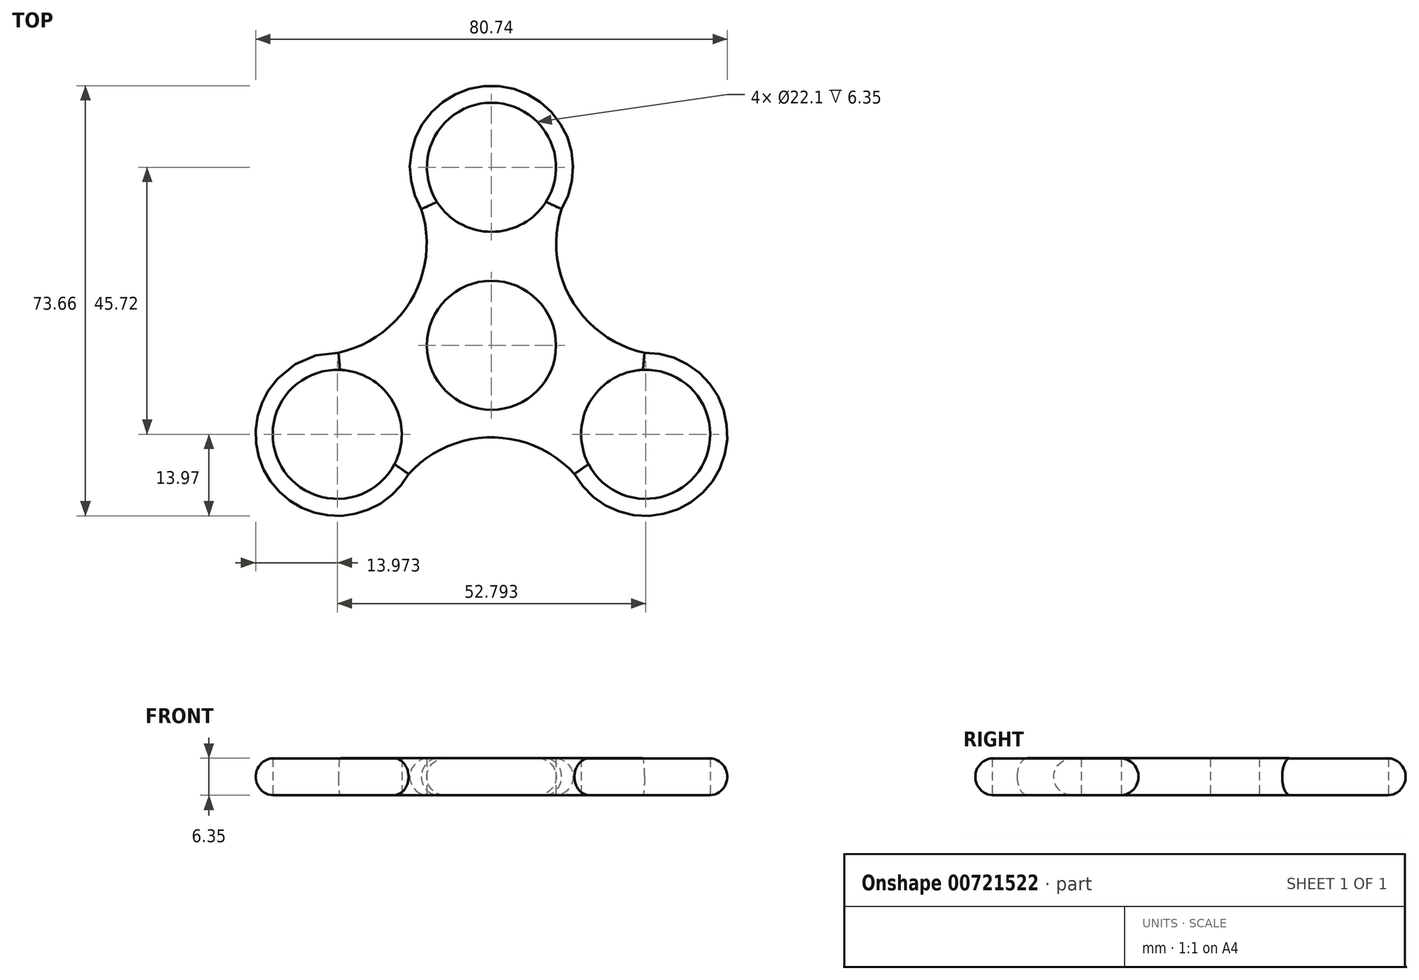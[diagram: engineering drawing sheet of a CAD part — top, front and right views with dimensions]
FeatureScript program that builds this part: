
annotation { "Feature Type Name" : "Feature", "Feature Type Description" : "" }
export const myFeature = defineFeature(function(context is Context, id is Id, definition is map)
    precondition{}
    {
        {
            var Q0;
            Q0=qCreatedBy(makeId("Top.planeOp"),FACE);
            var sketch = newSketch(context, id + "F0", { "sketchPlane" : qUnion([Q0])});
            skCircle(sketch, "E0", {"center": v(0, 0) * mm, "radius": 11.05 * mm});
            skLineSegment(sketch, "E1", {"start": v(0, 0) * mm, "end": v(0, 30.48) * mm});
            skCircle(sketch, "E2", {"center": v(0, 30.48) * mm, "radius": 11.05 * mm});
            skArc(sketch, "E3", {"start": v(12, 23.32) * mm, "mid": v(0, 44.45) * mm, "end": v(-12, 23.32) * mm});
            skCircle(sketch, "E4.1.0", {"center": v(-26.4, -15.24) * mm, "radius": 11.05 * mm});
            skArc(sketch, "E4.1.1", {"start": v(-26.2, -1.27) * mm, "mid": v(-38.5, -22.22) * mm, "end": v(-14.2, -22.05) * mm});
            skCircle(sketch, "E4.2.0", {"center": v(26.4, -15.24) * mm, "radius": 11.05 * mm});
            skArc(sketch, "E4.2.1", {"start": v(14.2, -22.05) * mm, "mid": v(38.5, -22.23) * mm, "end": v(26.2, -1.27) * mm});
            skArc(sketch, "E5", {"start": v(-29.85, -1.7) * mm, "mid": v(-13.65, 7.88) * mm, "end": v(-13.45, 26.7) * mm});
            skPoint(sketch, "E6.orphan", {"position": v(-60.52, 34.94) * mm});
            skArc(sketch, "E7.1.0", {"start": v(16.4, -25) * mm, "mid": v(0, -15.76) * mm, "end": v(-16.4, -25) * mm});
            skArc(sketch, "E7.2.0", {"start": v(13.45, 26.7) * mm, "mid": v(13.65, 7.88) * mm, "end": v(29.85, -1.7) * mm});
            skSolve(sketch);
        }
        {
            var Q0;
            Q0 = qSketchRegion(id + "F0", true);
            extrude(context, id + "F1", {"entities" : qUnion([Q0]), "depth" : 6.35 * mm, "offsetDistance" : 25.4 * mm});
        }
        {
            var Q0;
            Q0=makeQuery(id+"F1.opExtrude","CAP_EDGE",EDGE,{"disambiguationData":[OSD([sQuery(id+"F0.wireOp",EDGE,"E3")])],"isStart":false});
            var Q1;
            Q1=makeQuery(id+"F1.opExtrude","CAP_EDGE",EDGE,{"disambiguationData":[OSD([sQuery(id+"F0.wireOp",EDGE,"E5")])],"isStart":false});
            var Q2;
            Q2=makeQuery(id+"F1.opExtrude","CAP_EDGE",EDGE,{"disambiguationData":[OSD([sQuery(id+"F0.wireOp",EDGE,"E7.2.0")])],"isStart":false});
            var Q3;
            Q3=makeQuery(id+"F1.opExtrude","CAP_EDGE",EDGE,{"disambiguationData":[OSD([sQuery(id+"F0.wireOp",EDGE,"E4.2.1")])],"isStart":false});
            var Q4;
            Q4=makeQuery(id+"F1.opExtrude","CAP_EDGE",EDGE,{"disambiguationData":[OSD([sQuery(id+"F0.wireOp",EDGE,"E4.1.1")])],"isStart":false});
            var Q5;
            Q5=makeQuery(id+"F1.opExtrude","CAP_EDGE",EDGE,{"disambiguationData":[OSD([sQuery(id+"F0.wireOp",EDGE,"E7.1.0")])],"isStart":false});
            var Q6;
            Q6=makeQuery(id+"F1.opExtrude","CAP_EDGE",EDGE,{"disambiguationData":[OSD([sQuery(id+"F0.wireOp",EDGE,"E3")])],"isStart":true});
            var Q7;
            Q7=makeQuery(id+"F1.opExtrude","CAP_EDGE",EDGE,{"disambiguationData":[OSD([sQuery(id+"F0.wireOp",EDGE,"E5")])],"isStart":true});
            var Q8;
            Q8=makeQuery(id+"F1.opExtrude","CAP_EDGE",EDGE,{"disambiguationData":[OSD([sQuery(id+"F0.wireOp",EDGE,"E4.1.1")])],"isStart":true});
            var Q9;
            Q9=makeQuery(id+"F1.opExtrude","CAP_EDGE",EDGE,{"disambiguationData":[OSD([sQuery(id+"F0.wireOp",EDGE,"E7.1.0")])],"isStart":true});
            var Q10;
            Q10=makeQuery(id+"F1.opExtrude","CAP_EDGE",EDGE,{"disambiguationData":[OSD([sQuery(id+"F0.wireOp",EDGE,"E4.2.1")])],"isStart":true});
            var Q11;
            Q11=makeQuery(id+"F1.opExtrude","CAP_EDGE",EDGE,{"disambiguationData":[OSD([sQuery(id+"F0.wireOp",EDGE,"E7.2.0")])],"isStart":true});
            fillet(context, id + "F2", {"entities" : qUnion([Q0, Q1, Q2, Q3, Q4, Q5, Q6, Q7, Q8, Q9, Q10, Q11]), "radius" : 3.17 * mm, "tangentPropagation" : true, "allowEdgeOverflow" : false});
        }
    });
